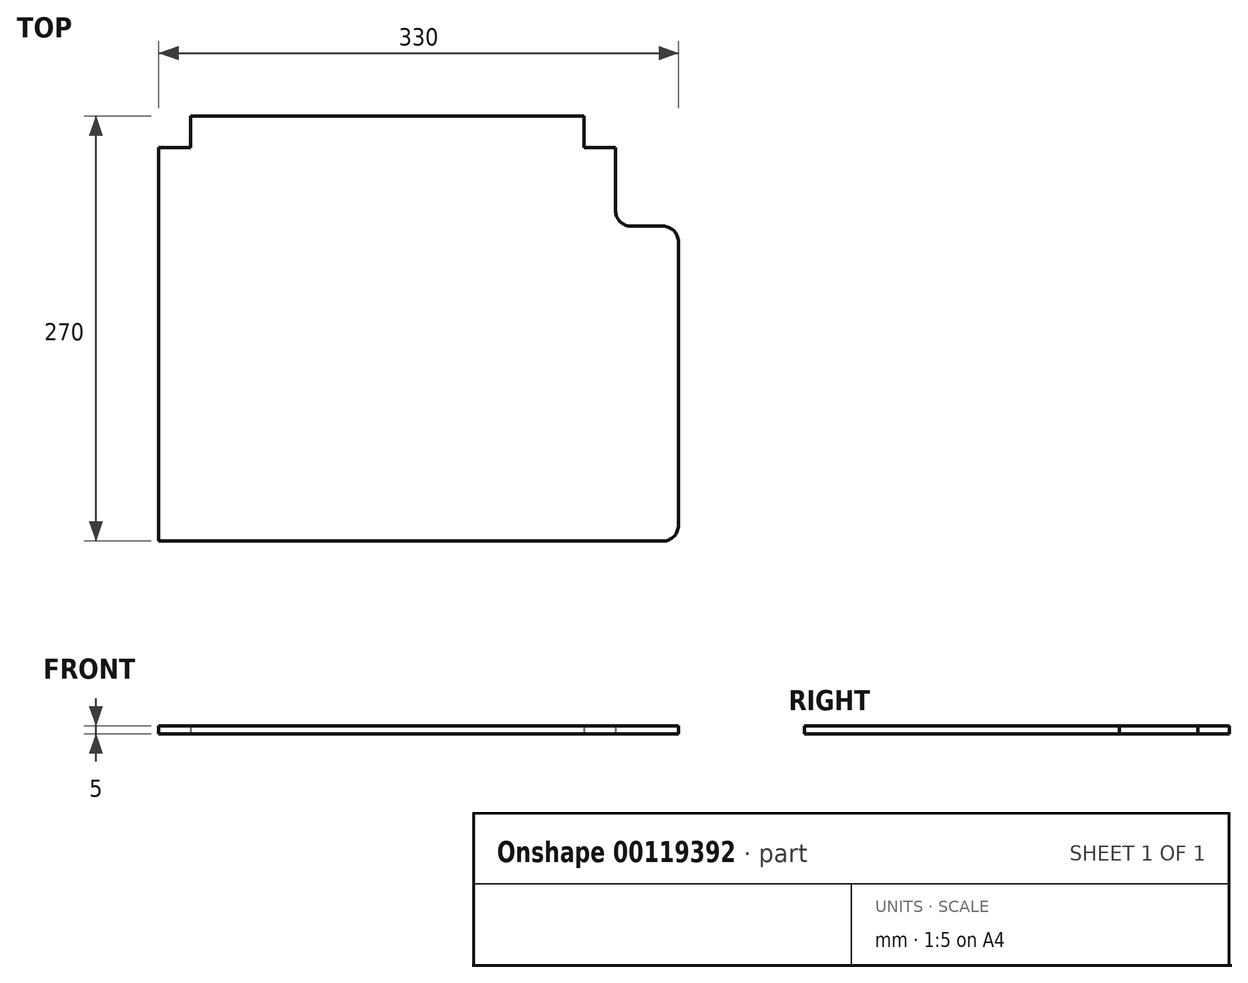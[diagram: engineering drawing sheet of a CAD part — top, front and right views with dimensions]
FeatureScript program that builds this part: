
annotation { "Feature Type Name" : "Feature", "Feature Type Description" : "" }
export const myFeature = defineFeature(function(context is Context, id is Id, definition is map)
    precondition{}
    {
        {
            var Q0;
            Q0=qCreatedBy(makeId("Top.planeOp"),FACE);
            var sketch = newSketch(context, id + "F0", { "sketchPlane" : qUnion([Q0])});
            skLineSegment(sketch, "E0.bottom", {"start": v(145, -125) * mm, "end": v(-145, -125) * mm});
            skLineSegment(sketch, "E0.top", {"start": v(145, 125) * mm, "end": v(125, 125) * mm});
            skLineSegment(sketch, "E0.left", {"start": v(145, 75) * mm, "end": v(145, 125) * mm});
            skLineSegment(sketch, "E0.right", {"start": v(-145, -125) * mm, "end": v(-145, 125) * mm});
            skPoint(sketch, "E0.middle", {"position": v(0, 0) * mm});
            skLineSegment(sketch, "E1.left", {"start": v(-125, 125) * mm, "end": v(-125, 145) * mm});
            skLineSegment(sketch, "E1.right", {"start": v(125, 125) * mm, "end": v(125, 145) * mm});
            skLineSegment(sketch, "E2.trimOffspring", {"start": v(-125, 125) * mm, "end": v(-145, 125) * mm});
            skLineSegment(sketch, "E3", {"start": v(-125, 145) * mm, "end": v(125, 145) * mm});
            skLineSegment(sketch, "E4.bottom", {"start": v(145, -125) * mm, "end": v(185, -125) * mm});
            skLineSegment(sketch, "E4.top", {"start": v(145, 75) * mm, "end": v(185, 75) * mm});
            skLineSegment(sketch, "E4.right", {"start": v(185, -125) * mm, "end": v(185, 75) * mm});
            skSolve(sketch);
        }
        {
            var Q0;
            Q0=makeQuery(id+"F0.imprint","IMPRINT",FACE,{"disambiguationData":[TD([[makeQuery(id+"F0.imprint","IMPRINT",EDGE,{"derivedFrom":sQuery(id+"F0.wireOp",EDGE,"E0.bottom")}),-1.0]])]});
            extrude(context, id + "F1", {"entities" : qUnion([Q0]), "depth" : 5 * mm});
        }
        {
            var Q0;
            Q0=makeQuery(id+"F1.opExtrude","SWEPT_EDGE",EDGE,{"disambiguationData":[OSD([sQuery(id+"F0.wireOp",EDGE,"E4.bottom"),sQuery(id+"F0.wireOp",EDGE,"E4.right")])]});
            var Q1;
            Q1=makeQuery(id+"F1.opExtrude","SWEPT_EDGE",EDGE,{"disambiguationData":[OSD([sQuery(id+"F0.wireOp",EDGE,"E4.top"),sQuery(id+"F0.wireOp",EDGE,"E4.right")])]});
            var Q2;
            Q2=makeQuery(id+"F1.opExtrude","SWEPT_EDGE",EDGE,{"disambiguationData":[OSD([sQuery(id+"F0.wireOp",EDGE,"E0.left"),sQuery(id+"F0.wireOp",EDGE,"E4.top")])]});
            fillet(context, id + "F2", {"entities" : qUnion([Q0, Q1, Q2]), "radius" : 10 * mm, "tangentPropagation" : true, "allowEdgeOverflow" : false});
        }
    });
